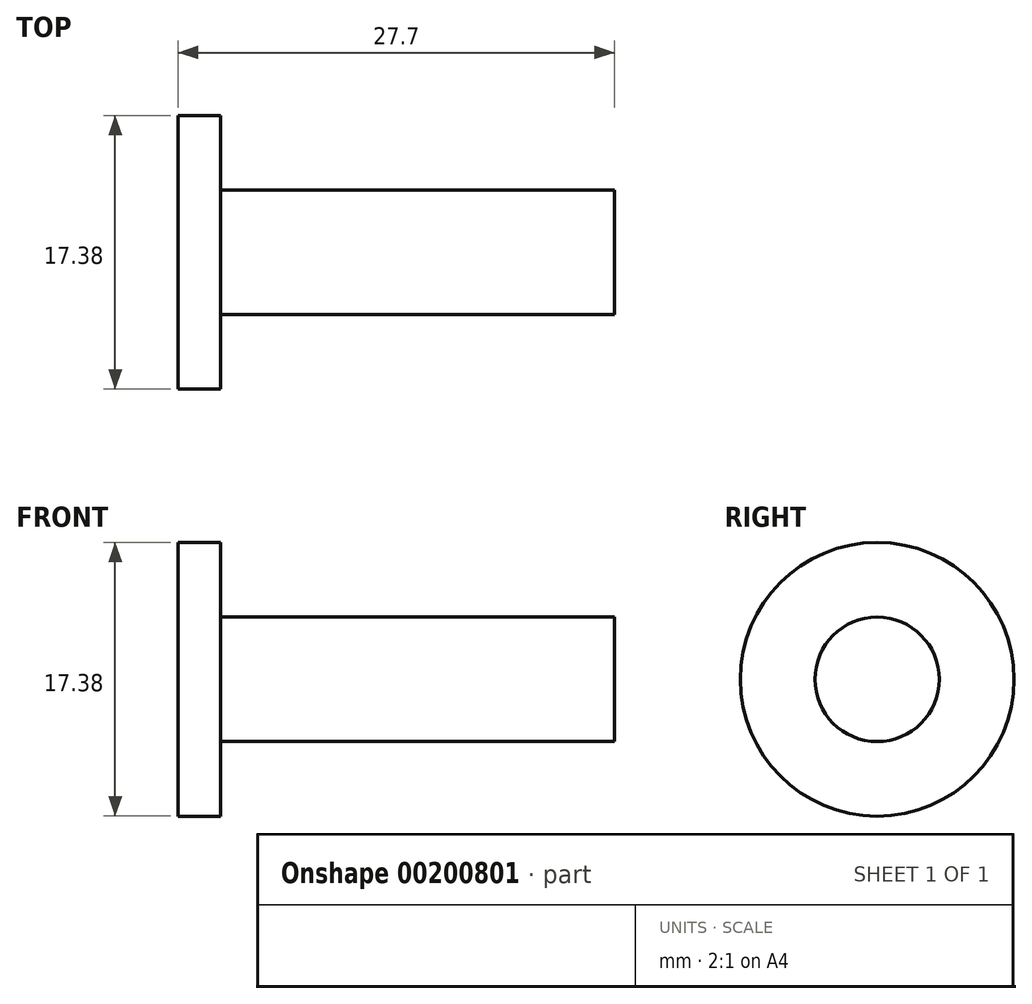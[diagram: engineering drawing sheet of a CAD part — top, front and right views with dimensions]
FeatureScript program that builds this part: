
annotation { "Feature Type Name" : "Feature", "Feature Type Description" : "" }
export const myFeature = defineFeature(function(context is Context, id is Id, definition is map)
    precondition{}
    {
        {
            var Q0;
            Q0=qCreatedBy(makeId("Right.planeOp"),FACE);
            var sketch = newSketch(context, id + "F0", { "sketchPlane" : qUnion([Q0])});
            skCircle(sketch, "E0", {"center": v(0, 0) * mm, "radius": 3.95 * mm});
            skSolve(sketch);
        }
        {
            var Q0;
            Q0=makeQuery(id+"F0.imprint","IMPRINT",FACE,{"disambiguationData":[TD([[makeQuery(id+"F0.imprint","IMPRINT",EDGE,{"derivedFrom":sQuery(id+"F0.wireOp",EDGE,"E0")}),1.0]])]});
            extrude(context, id + "F1", {"entities" : qUnion([Q0]), "depth" : 25 * mm});
        }
        {
            var Q0;
            Q0=qCreatedBy(makeId("Right.planeOp"),FACE);
            var sketch = newSketch(context, id + "F2", { "sketchPlane" : qUnion([Q0])});
            skCircle(sketch, "E1", {"center": v(0, 0) * mm, "radius": 8.7 * mm});
            skSolve(sketch);
        }
        {
            var Q0;
            Q0=makeQuery(id+"F2.imprint","IMPRINT",FACE,{"disambiguationData":[TD([[makeQuery(id+"F2.imprint","IMPRINT",EDGE,{"derivedFrom":sQuery(id+"F2.wireOp",EDGE,"E1")}),1.0]])]});
            extrude(context, id + "F3", {"entities" : qUnion([Q0]), "operationType" : NewBodyOperationType.ADD, "oppositeDirection" : true, "depth" : 2.7 * mm});
        }
    });
